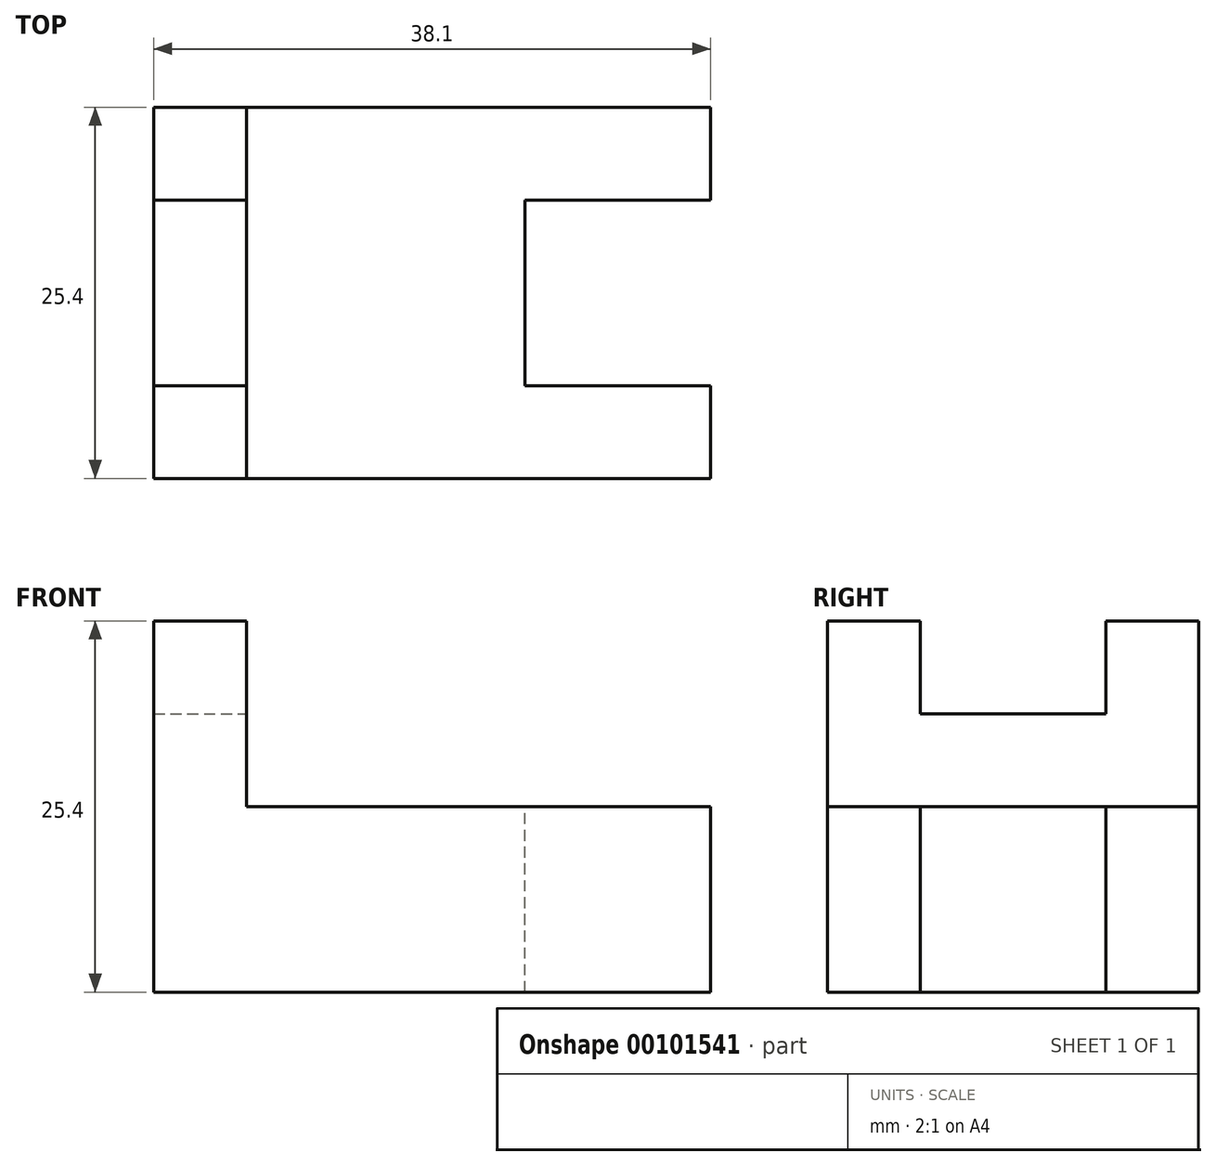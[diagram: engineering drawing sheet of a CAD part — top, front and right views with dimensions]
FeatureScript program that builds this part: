
annotation { "Feature Type Name" : "Feature", "Feature Type Description" : "" }
export const myFeature = defineFeature(function(context is Context, id is Id, definition is map)
    precondition{}
    {
        {
            var Q0;
            Q0=qCreatedBy(makeId("Front.planeOp"),FACE);
            var sketch = newSketch(context, id + "F0", { "sketchPlane" : qUnion([Q0])});
            skLineSegment(sketch, "E0", {"start": v(0, 0) * mm, "end": v(0, 25.4) * mm});
            skLineSegment(sketch, "E1", {"start": v(0, 25.4) * mm, "end": v(6.35, 25.4) * mm});
            skLineSegment(sketch, "E2", {"start": v(6.35, 25.4) * mm, "end": v(6.35, 12.7) * mm});
            skLineSegment(sketch, "E3", {"start": v(6.35, 12.7) * mm, "end": v(38.1, 12.7) * mm});
            skLineSegment(sketch, "E4", {"start": v(38.1, 12.7) * mm, "end": v(38.1, 0) * mm});
            skLineSegment(sketch, "E5", {"start": v(38.1, 0) * mm, "end": v(0, 0) * mm});
            skSolve(sketch);
        }
        {
            var Q0;
            Q0=makeQuery(id+"F0.imprint","IMPRINT",FACE,{"disambiguationData":[TD([[makeQuery(id+"F0.imprint","IMPRINT",EDGE,{"derivedFrom":sQuery(id+"F0.wireOp",EDGE,"E0")}),-1.0]])]});
            extrude(context, id + "F1", {"entities" : qUnion([Q0]), "oppositeDirection" : true, "depth" : 25.4 * mm});
        }
        {
            var Q0;
            Q0=makeQuery(id+"F1.opExtrude","SWEPT_FACE",FACE,{"disambiguationData":[OSD([sQuery(id+"F0.wireOp",EDGE,"E2")])]});
            var sketch = newSketch(context, id + "F2", { "sketchPlane" : qUnion([Q0])});
            skPoint(sketch, "E6.oppositeSnap0", {"position": v(0, 19.05) * mm});
            skLineSegment(sketch, "E7.bottom", {"start": v(6.35, 25.4) * mm, "end": v(19.05, 25.4) * mm});
            skLineSegment(sketch, "E7.top", {"start": v(6.35, 19.05) * mm, "end": v(19.05, 19.05) * mm});
            skLineSegment(sketch, "E7.left", {"start": v(6.35, 25.4) * mm, "end": v(6.35, 19.05) * mm});
            skLineSegment(sketch, "E7.right", {"start": v(19.05, 25.4) * mm, "end": v(19.05, 19.05) * mm});
            skSolve(sketch);
        }
        {
            var Q0;
            Q0=makeQuery(id+"F2.imprint","IMPRINT",FACE,{"disambiguationData":[TD([[makeQuery(id+"F2.imprint","IMPRINT",EDGE,{"derivedFrom":sQuery(id+"F2.wireOp",EDGE,"E7.bottom")}),1.0]])]});
            extrude(context, id + "F3", {"entities" : qUnion([Q0]), "operationType" : NewBodyOperationType.REMOVE, "endBound" : BoundingType.THROUGH_ALL, "oppositeDirection" : true, "depth" : 25.4 * mm});
        }
        {
            var Q0;
            Q0=makeQuery(id+"F1.opExtrude","SWEPT_FACE",FACE,{"disambiguationData":[OSD([sQuery(id+"F0.wireOp",EDGE,"E3")])]});
            var sketch = newSketch(context, id + "F4", { "sketchPlane" : qUnion([Q0])});
            skLineSegment(sketch, "E8", {"start": v(38.1, 6.35) * mm, "end": v(25.4, 6.35) * mm});
            skLineSegment(sketch, "E9", {"start": v(25.4, 6.35) * mm, "end": v(25.4, 19.05) * mm});
            skLineSegment(sketch, "E10", {"start": v(25.4, 19.05) * mm, "end": v(38.1, 19.05) * mm});
            skSolve(sketch);
        }
        {
            var Q0;
            {var subQ0=sQuery(id+"F4.wireOp",EDGE,"E8");Q0=makeQuery(id+"F4.imprint","IMPRINT",FACE,{"disambiguationData":[TD([[makeQuery(id+"F4.imprint","IMPRINT",EDGE,{"derivedFrom":subQ0}),-1.0]])]});}
            extrude(context, id + "F5", {"entities" : qUnion([Q0]), "operationType" : NewBodyOperationType.REMOVE, "endBound" : BoundingType.THROUGH_ALL, "oppositeDirection" : true, "depth" : 25.4 * mm});
        }
    });
